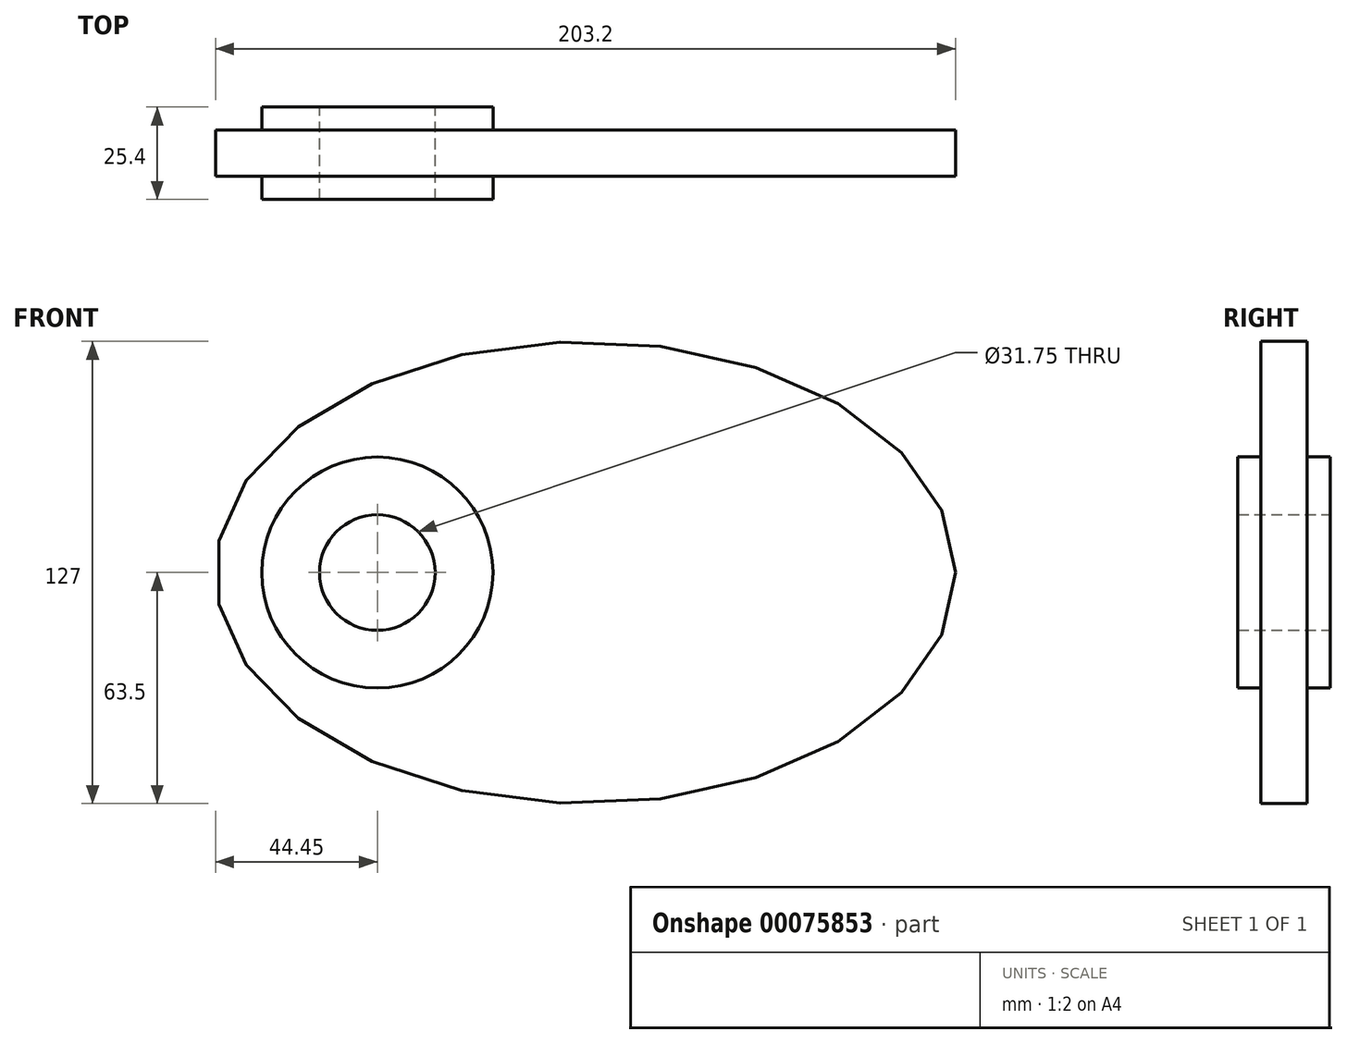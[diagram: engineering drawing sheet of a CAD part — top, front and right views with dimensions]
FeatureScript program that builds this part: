
annotation { "Feature Type Name" : "Feature", "Feature Type Description" : "" }
export const myFeature = defineFeature(function(context is Context, id is Id, definition is map)
    precondition{}
    {
        {
            var Q0;
            Q0=qCreatedBy(makeId("Front.planeOp"),FACE);
            var sketch = newSketch(context, id + "F0", { "sketchPlane" : qUnion([Q0])});
            skCircle(sketch, "E0", {"center": v(0, 0) * mm, "radius": 15.88 * mm});
            skCircle(sketch, "E1", {"center": v(0, 0) * mm, "radius": 31.75 * mm});
            skSolve(sketch);
        }
        {
            var Q0;
            Q0 = qSketchRegion(id + "F0", true);
            extrude(context, id + "F1", {"entities" : qUnion([Q0]), "endBound" : BoundingType.SYMMETRIC, "depth" : 25.4 * mm});
        }
        {
            var Q0;
            Q0=qCreatedBy(makeId("Front.planeOp"),FACE);
            var sketch = newSketch(context, id + "F2", { "sketchPlane" : qUnion([Q0])});
            skLineSegment(sketch, "E2", {"start": v(0, 0) * mm, "end": v(57.15, 0) * mm, "construction": true});
            skEllipse(sketch, "E3", {"center": v(57.15, 0) * mm, "majorRadius": 101.6 * mm, "minorRadius": 63.5 * mm, "majorAxis": v(1, 0)});
            skLineSegment(sketch, "E4", {"start": v(57.15, 63.5) * mm, "end": v(57.15, 0) * mm, "construction": true});
            skLineSegment(sketch, "E5", {"start": v(57.15, 0) * mm, "end": v(158.75, 0) * mm, "construction": true});
            skFitSpline(sketch, "E6.0", {"points": [v(142.82, -1.9) * mm, v(142.9, 0) * mm, v(142.82, 1.9) * mm, v(142.52, 4.41) * mm, v(141.77, 7.6) * mm, v(140.2, 11.5) * mm, v(137.91, 15.52) * mm, v(134.84, 19.6) * mm, v(130.96, 23.66) * mm, v(127.04, 26.98) * mm, v(123.48, 29.56) * mm, v(120.6, 31.45) * mm, v(117.55, 33.27) * mm, v(113.26, 35.58) * mm, v(107.5, 38.25) * mm, v(100.05, 41.03) * mm, v(92.12, 43.38) * mm, v(83.79, 45.24) * mm, v(76.58, 46.38) * mm, v(70.69, 47.02) * mm, v(66.22, 47.37) * mm, v(62.45, 47.54) * mm, v(59.43, 47.61) * mm, v(57.15, 47.63) * mm, v(54.87, 47.61) * mm, v(51.85, 47.54) * mm, v(48.08, 47.37) * mm, v(43.61, 47.02) * mm, v(37.72, 46.38) * mm, v(30.51, 45.24) * mm, v(22.18, 43.38) * mm, v(14.25, 41.03) * mm, v(6.8, 38.25) * mm, v(1.04, 35.58) * mm, v(-3.25, 33.27) * mm, v(-6.3, 31.45) * mm, v(-9.18, 29.56) * mm, v(-12.74, 26.98) * mm, v(-16.66, 23.66) * mm, v(-20.54, 19.6) * mm, v(-23.61, 15.52) * mm, v(-25.9, 11.5) * mm, v(-27.47, 7.6) * mm, v(-28.22, 4.41) * mm, v(-28.52, 1.9) * mm, v(-28.6, 0) * mm, v(-28.52, -1.9) * mm, v(-28.22, -4.41) * mm, v(-27.47, -7.6) * mm, v(-25.9, -11.5) * mm, v(-23.61, -15.52) * mm, v(-20.54, -19.6) * mm, v(-16.66, -23.66) * mm, v(-12.74, -26.98) * mm, v(-9.18, -29.56) * mm, v(-6.3, -31.45) * mm, v(-3.25, -33.27) * mm, v(1.04, -35.58) * mm, v(6.8, -38.25) * mm, v(14.25, -41.03) * mm, v(22.18, -43.38) * mm, v(30.51, -45.24) * mm, v(37.72, -46.38) * mm, v(43.61, -47.02) * mm, v(48.08, -47.37) * mm, v(51.85, -47.54) * mm, v(54.87, -47.61) * mm, v(57.15, -47.63) * mm, v(59.43, -47.61) * mm, v(62.45, -47.54) * mm, v(66.22, -47.37) * mm, v(70.69, -47.02) * mm, v(76.58, -46.38) * mm, v(83.79, -45.24) * mm, v(92.12, -43.38) * mm, v(100.05, -41.03) * mm, v(107.5, -38.25) * mm, v(113.26, -35.58) * mm, v(117.55, -33.27) * mm, v(120.6, -31.45) * mm, v(123.48, -29.56) * mm, v(127.04, -26.98) * mm, v(130.96, -23.66) * mm, v(134.84, -19.6) * mm, v(137.91, -15.52) * mm, v(140.2, -11.5) * mm, v(141.77, -7.6) * mm, v(142.52, -4.41) * mm, v(142.82, -1.9) * mm, v(142.9, 0) * mm, v(142.82, 1.9) * mm]});
            skLineSegment(sketch, "E7", {"start": v(39.37, 7.94) * mm, "end": v(113.9, 7.94) * mm, "construction": true});
            skArc(sketch, "E8", {"start": v(113.9, 7.94) * mm, "mid": v(126.1, 17.13) * mm, "end": v(120.64, 31.4) * mm, "construction": true});
            skArc(sketch, "E9.0", {"start": v(28.12, 14.74) * mm, "mid": v(25.34, 19.13) * mm, "end": v(21.87, 23.01) * mm, "construction": true});
            skArc(sketch, "E10", {"start": v(28.12, 14.74) * mm, "mid": v(32.8, 9.77) * mm, "end": v(39.37, 7.94) * mm, "construction": true});
            skArc(sketch, "E11", {"start": v(28, 44.65) * mm, "mid": v(18.4, 35.68) * mm, "end": v(21.87, 23.01) * mm, "construction": true});
            skArc(sketch, "E12.MirrorCS", {"start": v(28, -44.65) * mm, "mid": v(18.4, -35.68) * mm, "end": v(21.87, -23.01) * mm, "construction": true});
            skArc(sketch, "E13.MirrorCS", {"start": v(28.12, -14.74) * mm, "mid": v(32.8, -9.77) * mm, "end": v(39.37, -7.94) * mm, "construction": true});
            skArc(sketch, "E14.MirrorCS", {"start": v(28.12, -14.74) * mm, "mid": v(25.34, -19.13) * mm, "end": v(21.87, -23.01) * mm, "construction": true});
            skLineSegment(sketch, "E15.MirrorCS", {"start": v(39.37, -7.94) * mm, "end": v(113.9, -7.94) * mm, "construction": true});
            skArc(sketch, "E16.MirrorCS", {"start": v(113.9, -7.94) * mm, "mid": v(126.1, -17.13) * mm, "end": v(120.64, -31.4) * mm, "construction": true});
            skFitSpline(sketch, "E17.0", {"points": [v(142.82, -1.9) * mm, v(142.9, 0) * mm, v(142.82, 1.9) * mm, v(142.52, 4.41) * mm, v(141.77, 7.6) * mm, v(140.2, 11.5) * mm, v(137.91, 15.52) * mm, v(134.84, 19.6) * mm, v(130.96, 23.66) * mm, v(127.04, 26.98) * mm, v(123.48, 29.56) * mm, v(120.6, 31.45) * mm, v(117.55, 33.27) * mm, v(113.26, 35.58) * mm, v(107.5, 38.25) * mm, v(100.05, 41.03) * mm, v(92.12, 43.38) * mm, v(83.79, 45.24) * mm, v(76.58, 46.38) * mm, v(70.69, 47.02) * mm, v(66.22, 47.37) * mm, v(62.45, 47.54) * mm, v(59.43, 47.61) * mm, v(57.15, 47.63) * mm, v(54.87, 47.61) * mm, v(51.85, 47.54) * mm, v(48.08, 47.37) * mm, v(43.61, 47.02) * mm, v(37.72, 46.38) * mm, v(30.51, 45.24) * mm, v(22.18, 43.38) * mm, v(14.25, 41.03) * mm, v(6.8, 38.25) * mm, v(1.04, 35.58) * mm, v(-3.25, 33.27) * mm, v(-6.3, 31.45) * mm, v(-9.18, 29.56) * mm, v(-12.74, 26.98) * mm, v(-16.66, 23.66) * mm, v(-20.54, 19.6) * mm, v(-23.61, 15.52) * mm, v(-25.9, 11.5) * mm, v(-27.47, 7.6) * mm, v(-28.22, 4.41) * mm, v(-28.52, 1.9) * mm, v(-28.6, 0) * mm, v(-28.52, -1.9) * mm, v(-28.22, -4.41) * mm, v(-27.47, -7.6) * mm, v(-25.9, -11.5) * mm, v(-23.61, -15.52) * mm, v(-20.54, -19.6) * mm, v(-16.66, -23.66) * mm, v(-12.74, -26.98) * mm, v(-9.18, -29.56) * mm, v(-6.3, -31.45) * mm, v(-3.25, -33.27) * mm, v(1.04, -35.58) * mm, v(6.8, -38.25) * mm, v(14.25, -41.03) * mm, v(22.18, -43.38) * mm, v(30.51, -45.24) * mm, v(37.72, -46.38) * mm, v(43.61, -47.02) * mm, v(48.08, -47.37) * mm, v(51.85, -47.54) * mm, v(54.87, -47.61) * mm, v(57.15, -47.63) * mm, v(59.43, -47.61) * mm, v(62.45, -47.54) * mm, v(66.22, -47.37) * mm, v(70.69, -47.02) * mm, v(76.58, -46.38) * mm, v(83.79, -45.24) * mm, v(92.12, -43.38) * mm, v(100.05, -41.03) * mm, v(107.5, -38.25) * mm, v(113.26, -35.58) * mm, v(117.55, -33.27) * mm, v(120.6, -31.45) * mm, v(123.48, -29.56) * mm, v(127.04, -26.98) * mm, v(130.96, -23.66) * mm, v(134.84, -19.6) * mm, v(137.91, -15.52) * mm, v(140.2, -11.5) * mm, v(141.77, -7.6) * mm, v(142.52, -4.41) * mm, v(142.82, -1.9) * mm, v(142.9, 0) * mm, v(142.82, 1.9) * mm], "construction": true});
            skFitSpline(sketch, "E18.trimOffspring", {"points": [v(142.82, -1.9) * mm, v(142.9, 0) * mm, v(142.82, 1.9) * mm, v(142.52, 4.41) * mm, v(141.77, 7.6) * mm, v(140.2, 11.5) * mm, v(137.91, 15.52) * mm, v(134.84, 19.6) * mm, v(130.96, 23.66) * mm, v(127.04, 26.98) * mm, v(123.48, 29.56) * mm, v(120.6, 31.45) * mm, v(117.55, 33.27) * mm, v(113.26, 35.58) * mm, v(107.5, 38.25) * mm, v(100.05, 41.03) * mm, v(92.12, 43.38) * mm, v(83.79, 45.24) * mm, v(76.58, 46.38) * mm, v(70.69, 47.02) * mm, v(66.22, 47.37) * mm, v(62.45, 47.54) * mm, v(59.43, 47.61) * mm, v(57.15, 47.63) * mm, v(54.87, 47.61) * mm, v(51.85, 47.54) * mm, v(48.08, 47.37) * mm, v(43.61, 47.02) * mm, v(37.72, 46.38) * mm, v(30.51, 45.24) * mm, v(22.18, 43.38) * mm, v(14.25, 41.03) * mm, v(6.8, 38.25) * mm, v(1.04, 35.58) * mm, v(-3.25, 33.27) * mm, v(-6.3, 31.45) * mm, v(-9.18, 29.56) * mm, v(-12.74, 26.98) * mm, v(-16.66, 23.66) * mm, v(-20.54, 19.6) * mm, v(-23.61, 15.52) * mm, v(-25.9, 11.5) * mm, v(-27.47, 7.6) * mm, v(-28.22, 4.41) * mm, v(-28.52, 1.9) * mm, v(-28.6, 0) * mm, v(-28.52, -1.9) * mm, v(-28.22, -4.41) * mm, v(-27.47, -7.6) * mm, v(-25.9, -11.5) * mm, v(-23.61, -15.52) * mm, v(-20.54, -19.6) * mm, v(-16.66, -23.66) * mm, v(-12.74, -26.98) * mm, v(-9.18, -29.56) * mm, v(-6.3, -31.45) * mm, v(-3.25, -33.27) * mm, v(1.04, -35.58) * mm, v(6.8, -38.25) * mm, v(14.25, -41.03) * mm, v(22.18, -43.38) * mm, v(30.51, -45.24) * mm, v(37.72, -46.38) * mm, v(43.61, -47.02) * mm, v(48.08, -47.37) * mm, v(51.85, -47.54) * mm, v(54.87, -47.61) * mm, v(57.15, -47.63) * mm, v(59.43, -47.61) * mm, v(62.45, -47.54) * mm, v(66.22, -47.37) * mm, v(70.69, -47.02) * mm, v(76.58, -46.38) * mm, v(83.79, -45.24) * mm, v(92.12, -43.38) * mm, v(100.05, -41.03) * mm, v(107.5, -38.25) * mm, v(113.26, -35.58) * mm, v(117.55, -33.27) * mm, v(120.6, -31.45) * mm, v(123.48, -29.56) * mm, v(127.04, -26.98) * mm, v(130.96, -23.66) * mm, v(134.84, -19.6) * mm, v(137.91, -15.52) * mm, v(140.2, -11.5) * mm, v(141.77, -7.6) * mm, v(142.52, -4.41) * mm, v(142.82, -1.9) * mm, v(142.9, 0) * mm, v(142.82, 1.9) * mm], "construction": true});
            skCircle(sketch, "E19.0", {"center": v(0, 0) * mm, "radius": 15.88 * mm});
            skSolve(sketch);
        }
        {
            var Q0;
            Q0 = qSketchRegion(id + "F2", true);
            extrude(context, id + "F3", {"entities" : qUnion([Q0]), "operationType" : NewBodyOperationType.ADD, "endBound" : BoundingType.SYMMETRIC, "depth" : 12.7 * mm});
        }
    });
